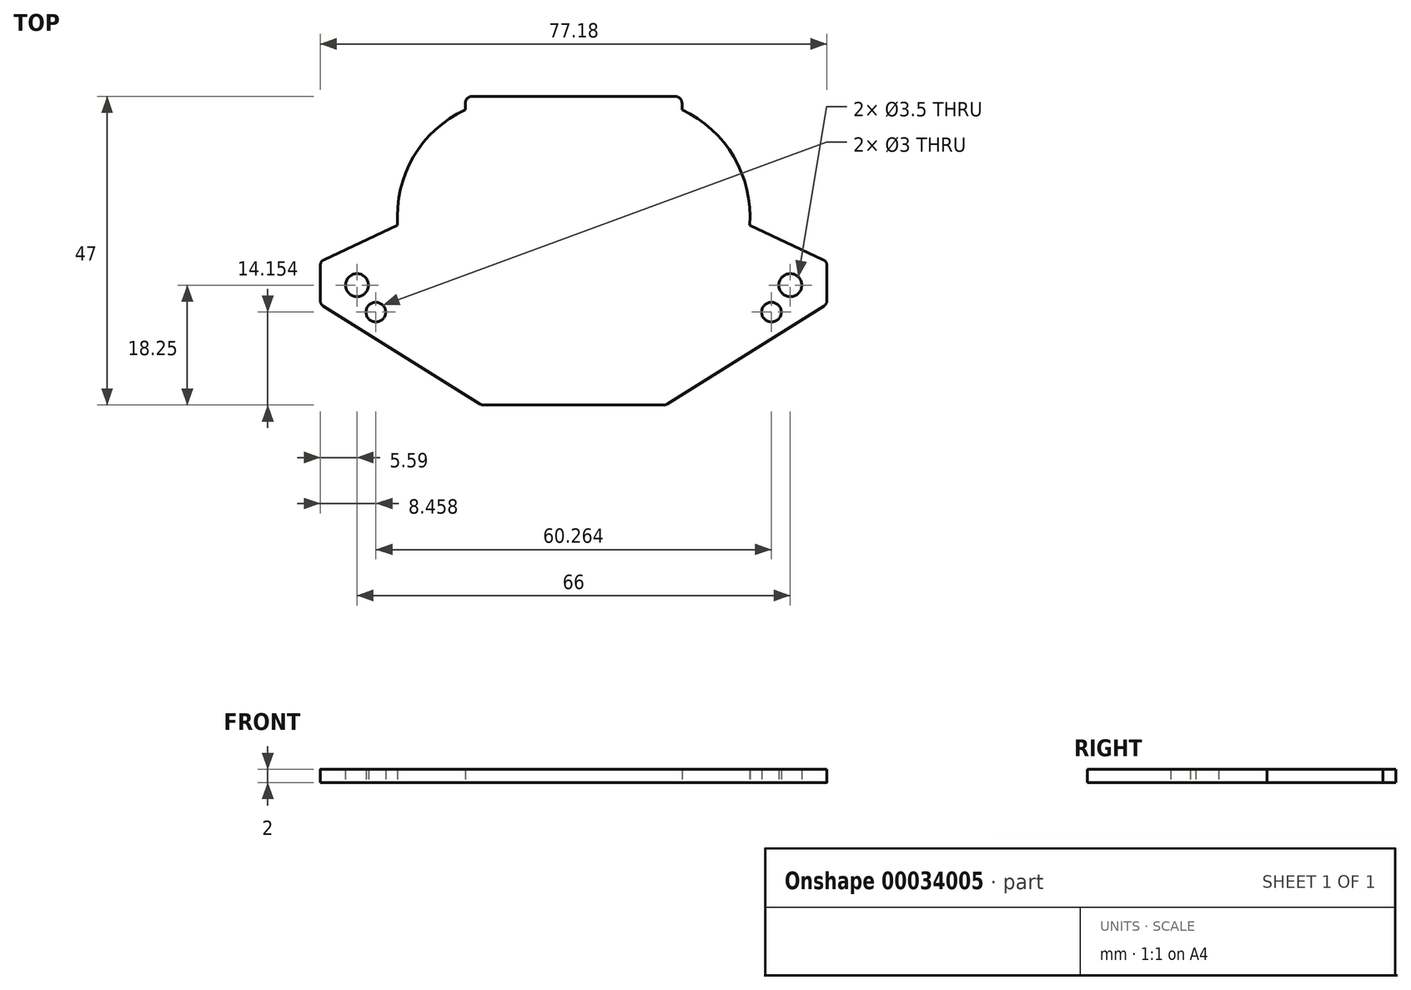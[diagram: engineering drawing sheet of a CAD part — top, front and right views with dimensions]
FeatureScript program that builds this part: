
annotation { "Feature Type Name" : "Feature", "Feature Type Description" : "" }
export const myFeature = defineFeature(function(context is Context, id is Id, definition is map)
    precondition{}
    {
        {
            var Q0;
            Q0=qCreatedBy(makeId("Top.planeOp"),FACE);
            var sketch = newSketch(context, id + "F0", { "sketchPlane" : qUnion([Q0])});
            skLineSegment(sketch, "E0", {"start": v(0, 0) * mm, "end": v(33, 0) * mm, "construction": true});
            skCircle(sketch, "E1", {"center": v(33, 0) * mm, "radius": 1.75 * mm});
            skLineSegment(sketch, "E2", {"start": v(0, 27) * mm, "end": v(0, 0) * mm, "construction": true});
            skCircle(sketch, "E3.MirrorC", {"center": v(-33, 0) * mm, "radius": 1.75 * mm});
            skLineSegment(sketch, "E4", {"start": v(33, 0) * mm, "end": v(30.13, -4.1) * mm, "construction": true});
            skCircle(sketch, "E5", {"center": v(30.13, -4.1) * mm, "radius": 1.5 * mm});
            skLineSegment(sketch, "E6", {"start": v(-33, 0) * mm, "end": v(-30.13, -4.1) * mm, "construction": true});
            skCircle(sketch, "E7", {"center": v(-30.13, -4.1) * mm, "radius": 1.5 * mm});
            skCircle(sketch, "E8", {"center": v(0, 27) * mm, "radius": 1.75 * mm, "construction": true});
            skLineSegment(sketch, "E9", {"start": v(0, 28.75) * mm, "end": v(15.5, 28.75) * mm});
            skLineSegment(sketch, "E10.MirrorCS", {"start": v(0, 28.75) * mm, "end": v(-15.5, 28.75) * mm});
            skLineSegment(sketch, "E11", {"start": v(0, 28.75) * mm, "end": v(0, -18.25) * mm, "construction": true});
            skLineSegment(sketch, "E12", {"start": v(0, -18.25) * mm, "end": v(13.71, -18.25) * mm});
            skLineSegment(sketch, "E13.MirrorCS", {"start": v(0, -18.25) * mm, "end": v(-13.71, -18.25) * mm});
            skLineSegment(sketch, "E14", {"start": v(14.24, -18.1) * mm, "end": v(38.12, -3.18) * mm});
            skLineSegment(sketch, "E15", {"start": v(38.6, -2.33) * mm, "end": v(38.6, 2.98) * mm});
            skLineSegment(sketch, "E16", {"start": v(16.5, 27.75) * mm, "end": v(16.5, 26.75) * mm});
            skLineSegment(sketch, "E17", {"start": v(38.02, 3.89) * mm, "end": v(26.81, 9.11) * mm});
            skArc(sketch, "E18", {"start": v(26.81, 9.11) * mm, "mid": v(24.4, 19.54) * mm, "end": v(16.5, 26.75) * mm});
            skLineSegment(sketch, "E19.MirrorCS", {"start": v(-16.5, 27.75) * mm, "end": v(-16.5, 26.75) * mm});
            skLineSegment(sketch, "E20.MirrorCS", {"start": v(-38.02, 3.89) * mm, "end": v(-26.81, 9.11) * mm});
            skLineSegment(sketch, "E21.MirrorCS", {"start": v(-38.6, -2.33) * mm, "end": v(-38.6, 2.98) * mm});
            skLineSegment(sketch, "E22.MirrorCS", {"start": v(-14.24, -18.1) * mm, "end": v(-38.12, -3.18) * mm});
            skArc(sketch, "E23.MirrorCS", {"start": v(-26.81, 9.11) * mm, "mid": v(-24.4, 19.54) * mm, "end": v(-16.5, 26.75) * mm});
            skPoint(sketch, "E24.visualSharp", {"position": v(-38.6, 3.62) * mm});
            skArc(sketch, "E24.filletArc", {"start": v(-38.02, 3.89) * mm, "mid": v(-38.44, 3.52) * mm, "end": v(-38.6, 2.98) * mm});
            skPoint(sketch, "E25.visualSharp", {"position": v(-38.6, -2.88) * mm});
            skArc(sketch, "E25.filletArc", {"start": v(-38.6, -2.33) * mm, "mid": v(-38.47, -2.81) * mm, "end": v(-38.12, -3.18) * mm});
            skPoint(sketch, "E26.visualSharp", {"position": v(38.6, 3.62) * mm});
            skArc(sketch, "E26.filletArc", {"start": v(38.6, 2.98) * mm, "mid": v(38.44, 3.52) * mm, "end": v(38.02, 3.89) * mm});
            skPoint(sketch, "E27.visualSharp", {"position": v(38.6, -2.88) * mm});
            skArc(sketch, "E27.filletArc", {"start": v(38.12, -3.18) * mm, "mid": v(38.47, -2.81) * mm, "end": v(38.6, -2.33) * mm});
            skPoint(sketch, "E28.visualSharp", {"position": v(-16.5, 28.75) * mm});
            skArc(sketch, "E28.filletArc", {"start": v(-15.5, 28.75) * mm, "mid": v(-16.2, 28.46) * mm, "end": v(-16.5, 27.75) * mm});
            skPoint(sketch, "E29.visualSharp", {"position": v(16.5, 28.75) * mm});
            skArc(sketch, "E29.filletArc", {"start": v(16.5, 27.75) * mm, "mid": v(16.2, 28.46) * mm, "end": v(15.5, 28.75) * mm});
            skPoint(sketch, "E30.visualSharp", {"position": v(-14, -18.25) * mm});
            skArc(sketch, "E30.filletArc", {"start": v(-14.24, -18.1) * mm, "mid": v(-13.99, -18.21) * mm, "end": v(-13.71, -18.25) * mm});
            skPoint(sketch, "E31.visualSharp", {"position": v(14, -18.25) * mm});
            skArc(sketch, "E31.filletArc", {"start": v(13.71, -18.25) * mm, "mid": v(13.99, -18.21) * mm, "end": v(14.24, -18.1) * mm});
            skLineSegment(sketch, "E32", {"start": v(-55.35, 28.75) * mm, "end": v(-55.35, 0) * mm, "construction": true});
            skLineSegment(sketch, "E33", {"start": v(-51.08, -18.25) * mm, "end": v(-51.08, 28.75) * mm, "construction": true});
            skLineSegment(sketch, "E34", {"start": v(-55.35, 0) * mm, "end": v(-55.35, -18.25) * mm, "construction": true});
            skSolve(sketch);
        }
        {
            var Q0;
            Q0=qSketchRegion(id+"F0",true);
            var Q1;
            {var subQ0=sQuery(id+"F0.wireOp",EDGE,"9eed6b1a-6eb9-42a3-a3d7-c3db641d5e96");Q1=makeQuery(id+"F0.imprint","IMPRINT",FACE,{"disambiguationData":[TD([[makeQuery(id+"F0.imprint","IMPRINT",EDGE,{"derivedFrom":subQ0}),-1.0]])]});}
            var Q2;
            {var subQ1=sQuery(id+"F0.wireOp",EDGE,"28da098a-489b-44c9-9874-73c2eb542d50");Q2=makeQuery(id+"F0.imprint","IMPRINT",FACE,{"disambiguationData":[TD([[makeQuery(id+"F0.imprint","IMPRINT",EDGE,{"derivedFrom":subQ1}),-1.0]])]});}
            var Q3;
            {var subQ0=sQuery(id+"F0.wireOp",EDGE,"3e13071a-8318-441f-badd-53a84b6dc6d1");Q3=makeQuery(id+"F0.imprint","IMPRINT",FACE,{"disambiguationData":[TD([[makeQuery(id+"F0.imprint","IMPRINT",EDGE,{"derivedFrom":subQ0}),-1.0]])]});}
            var Q4;
            {var subQ1=sQuery(id+"F0.wireOp",EDGE,"ca81a403-cbb4-4677-85eb-217c0f882b60");Q4=makeQuery(id+"F0.imprint","IMPRINT",FACE,{"disambiguationData":[TD([[makeQuery(id+"F0.imprint","IMPRINT",EDGE,{"derivedFrom":subQ1}),-1.0]])]});}
            var Q5;
            {var subQ1=sQuery(id+"F0.wireOp",EDGE,"62e1dda4-033d-4fcc-b43b-23b2ebeb439e");Q5=makeQuery(id+"F0.imprint","IMPRINT",FACE,{"disambiguationData":[TD([[makeQuery(id+"F0.imprint","IMPRINT",EDGE,{"derivedFrom":subQ1}),-1.0]])]});}
            extrude(context, id + "F1", {"entities" : qUnion([Q0, Q1, Q2, Q3, Q4, Q5]), "depth" : 2 * mm});
        }
    });
